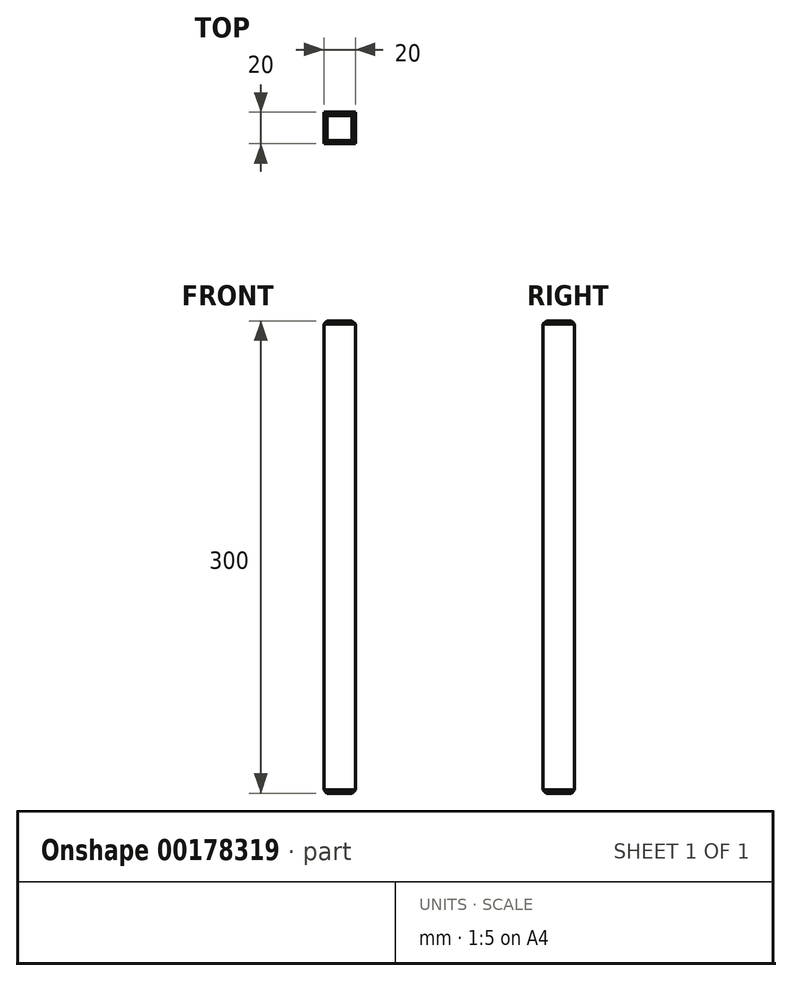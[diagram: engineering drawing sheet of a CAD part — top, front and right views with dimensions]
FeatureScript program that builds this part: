
annotation { "Feature Type Name" : "Feature", "Feature Type Description" : "" }
export const myFeature = defineFeature(function(context is Context, id is Id, definition is map)
    precondition{}
    {
        {
            var Q0;
            Q0=qCreatedBy(makeId("Top.planeOp"),FACE);
            var sketch = newSketch(context, id + "F0", { "sketchPlane" : qUnion([Q0])});
            skLineSegment(sketch, "E0.bottom", {"start": v(-10, 10) * mm, "end": v(10, 10) * mm});
            skLineSegment(sketch, "E0.top", {"start": v(-10, -10) * mm, "end": v(10, -10) * mm});
            skLineSegment(sketch, "E0.left", {"start": v(-10, 10) * mm, "end": v(-10, -10) * mm});
            skLineSegment(sketch, "E0.right", {"start": v(10, 10) * mm, "end": v(10, -10) * mm});
            skPoint(sketch, "E0.middle", {"position": v(0, 0) * mm});
            skSolve(sketch);
        }
        {
            var Q0;
            Q0 = qSketchRegion(id + "F0", true);
            extrude(context, id + "F1", {"entities" : qUnion([Q0]), "depth" : 300 * mm});
        }
        {
            var Q0;
            Q0=makeQuery(id+"F1.opExtrude","CAP_FACE",FACE,{"disambiguationData":[OSD([sQuery(id+"F0.wireOp",EDGE,"E0.bottom"),sQuery(id+"F0.wireOp",EDGE,"E0.top"),sQuery(id+"F0.wireOp",EDGE,"E0.left"),sQuery(id+"F0.wireOp",EDGE,"E0.right")])],"isStart":false});
            var Q1;
            Q1=makeQuery(id+"F1.opExtrude","CAP_FACE",FACE,{"disambiguationData":[OSD([sQuery(id+"F0.wireOp",EDGE,"E0.bottom"),sQuery(id+"F0.wireOp",EDGE,"E0.top"),sQuery(id+"F0.wireOp",EDGE,"E0.left"),sQuery(id+"F0.wireOp",EDGE,"E0.right")])],"isStart":true});
            chamfer(context, id + "F2", {"entities" : qUnion([Q0, Q1]), "width" : 2 * mm, "tangentPropagation" : true});
        }
    });
